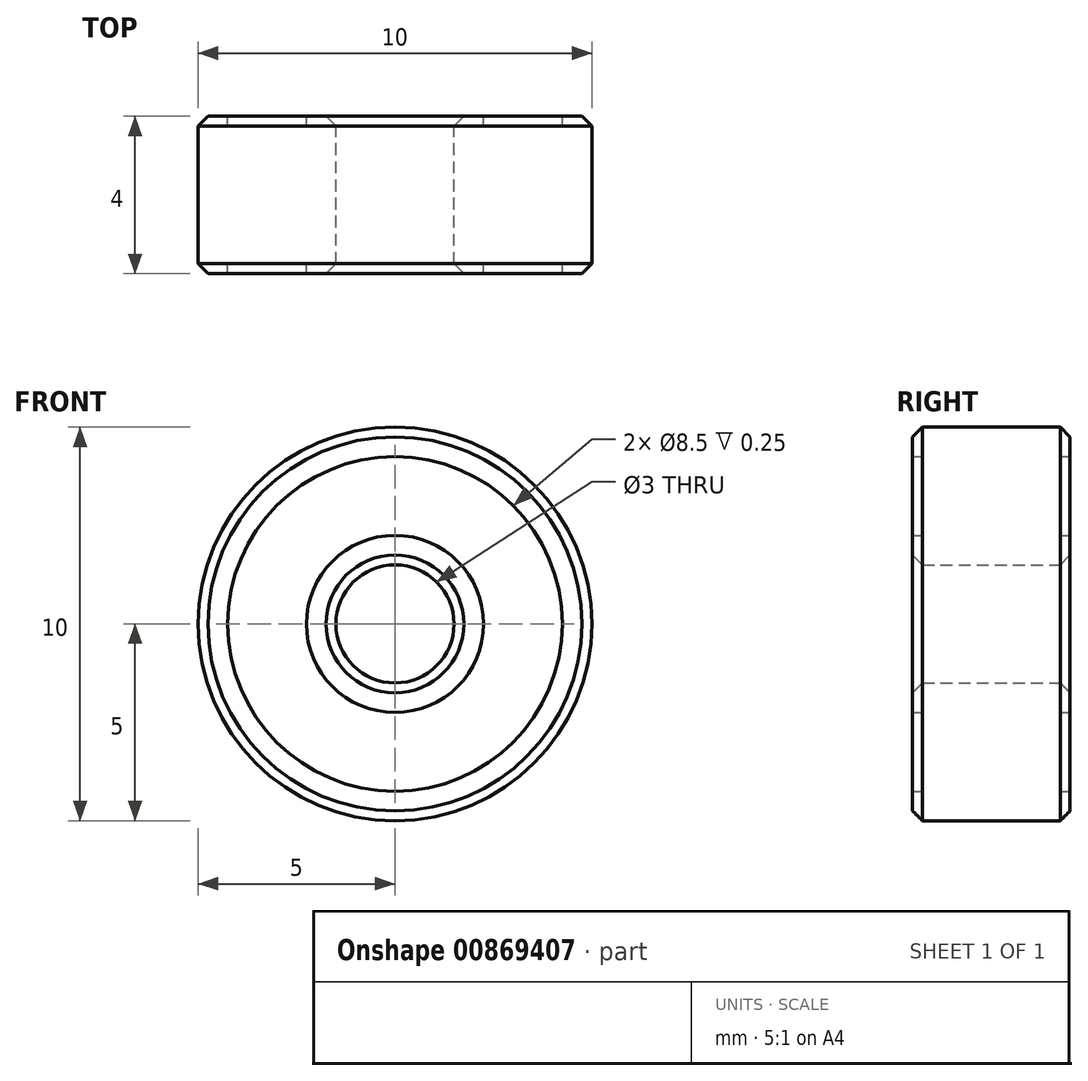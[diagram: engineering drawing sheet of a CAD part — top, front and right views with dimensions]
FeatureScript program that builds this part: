
annotation { "Feature Type Name" : "Feature", "Feature Type Description" : "" }
export const myFeature = defineFeature(function(context is Context, id is Id, definition is map)
    precondition{}
    {
        {
            var Q0;
            Q0=qCreatedBy(makeId("Front.planeOp"),FACE);
            var sketch = newSketch(context, id + "F0", { "sketchPlane" : qUnion([Q0])});
            skCircle(sketch, "E0", {"center": v(0, 0) * mm, "radius": 1.5 * mm});
            skCircle(sketch, "E1", {"center": v(0, 0) * mm, "radius": 5 * mm});
            skSolve(sketch);
        }
        {
            var Q0;
            Q0=makeQuery(id+"F0.imprint","IMPRINT",FACE,{"disambiguationData":[TD([[makeQuery(id+"F0.imprint","IMPRINT",EDGE,{"derivedFrom":sQuery(id+"F0.wireOp",EDGE,"E0")}),-1.0]])]});
            extrude(context, id + "F1", {"entities" : qUnion([Q0]), "depth" : 3.5 * mm, "offsetDistance" : 25 * mm});
        }
        {
            var Q0;
            Q0=makeQuery(id+"F1.opExtrude","CAP_FACE",FACE,{"disambiguationData":[OSD([sQuery(id+"F0.wireOp",EDGE,"E0"),sQuery(id+"F0.wireOp",EDGE,"E1")])],"isStart":false});
            var sketch = newSketch(context, id + "F2", { "sketchPlane" : qUnion([Q0])});
            skCircle(sketch, "E2", {"center": v(0, 0) * mm, "radius": 2.25 * mm});
            skCircle(sketch, "E3", {"center": v(0, 0) * mm, "radius": 4.25 * mm});
            skCircle(sketch, "E4.0", {"center": v(0, 0) * mm, "radius": 5 * mm});
            skCircle(sketch, "E5.0", {"center": v(0, 0) * mm, "radius": 1.5 * mm});
            skSolve(sketch);
        }
        {
            var Q0;
            Q0=makeQuery(id+"F2.imprint","IMPRINT",FACE,{"disambiguationData":[TD([[makeQuery(id+"F2.imprint","IMPRINT",EDGE,{"derivedFrom":sQuery(id+"F2.wireOp",EDGE,"E2")}),1.0]])]});
            var Q1;
            Q1=makeQuery(id+"F2.imprint","IMPRINT",FACE,{"disambiguationData":[TD([[makeQuery(id+"F2.imprint","IMPRINT",EDGE,{"derivedFrom":sQuery(id+"F2.wireOp",EDGE,"E3")}),-1.0]])]});
            extrude(context, id + "F3", {"entities" : qUnion([Q0, Q1]), "operationType" : NewBodyOperationType.ADD, "depth" : .25 * mm, "offsetDistance" : 25 * mm, "hasSecondDirection" : true, "secondDirectionOppositeDirection" : true, "secondDirectionDepth" : 3.75 * mm});
        }
        {
            var Q0;
            Q0=makeQuery(id+"F3.opExtrude","CAP_EDGE",EDGE,{"disambiguationData":[OSD([sQuery(id+"F2.wireOp",EDGE,"E4.0")])],"isStart":false});
            var Q1;
            Q1=makeQuery(id+"F3.opExtrude","CAP_EDGE",EDGE,{"disambiguationData":[OSD([sQuery(id+"F2.wireOp",EDGE,"E5.0")])],"isStart":false});
            var Q2;
            Q2=makeQuery(id+"F3.opExtrude","CAP_EDGE",EDGE,{"disambiguationData":[OSD([sQuery(id+"F2.wireOp",EDGE,"E5.0")])],"isStart":true});
            var Q3;
            Q3=makeQuery(id+"F3.opExtrude","CAP_EDGE",EDGE,{"disambiguationData":[OSD([sQuery(id+"F2.wireOp",EDGE,"E4.0")])],"isStart":true});
            chamfer(context, id + "F4", {"entities" : qUnion([Q0, Q1, Q2, Q3]), "width" : .25 * mm, "tangentPropagation" : true});
        }
    });
